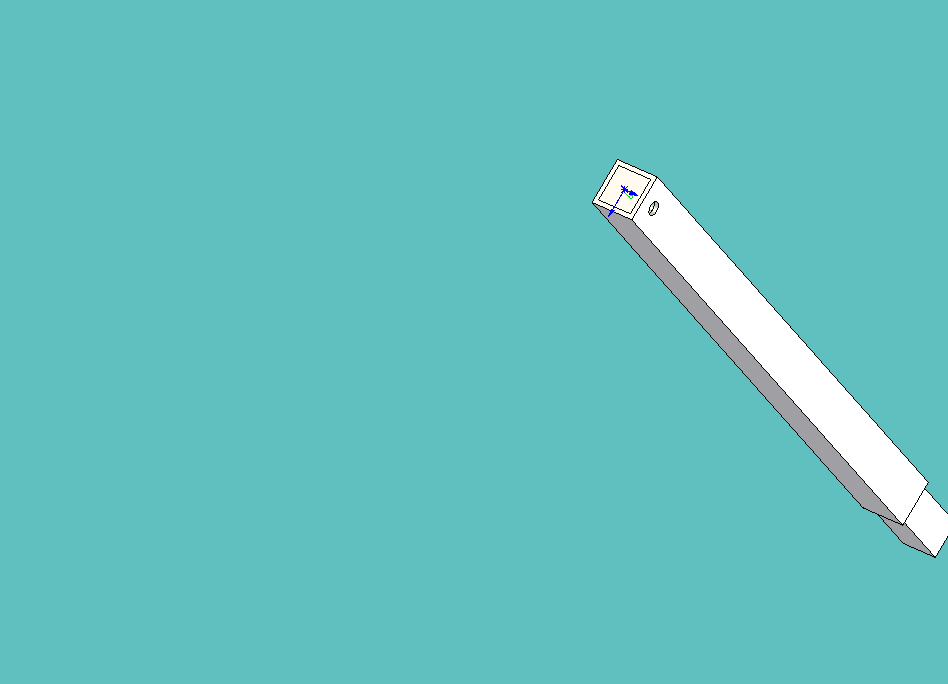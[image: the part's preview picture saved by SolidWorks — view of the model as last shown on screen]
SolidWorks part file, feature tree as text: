
SOLIDWORKS PART (.sldprt)
format: sldprt  version: not decoded by parser v0  size: 214,528 bytes
history: native  units: mm
features: sketch x5, extrude x3, cut_extrude x2, material x1 (+13 scaffold rows collapsed)
feature tree (24):
  scaffold x13  (default folders/planes/origin — collapsed)
  material  "Material <not specified>"
  sketch  "Sketch1"  dims[D1=31.75mm D2=31.75mm D3=15.875mm D4=15.875mm D5=3.175mm]
  extrude  "Extrude1"  Depth=457.2mm
  sketch  "Sketch2"  dims[D1=25.4mm]
  extrude  "Extrude2"  Depth=57.15mm
  sketch  "Sketch4"
  extrude  "Extrude4"  Depth=31.75mm
  sketch  "Sketch3"  dims[D1=9.398mm D2=15.24mm D3=15.875mm]
  cut_extrude  "Cut-Extrude3"  [1 undecoded]
  sketch  "Sketch5"  dims[D1=2.159mm D2=12.7mm D3=12.7mm]
  cut_extrude  "Cut-Extrude4"  Depth=15.24mm
decode coverage: 8 of 10 modeling features carry decoded parameters
note: 1 parameter value undecoded
note: suppression state not decoded; provenance and decode notes live in map.json
